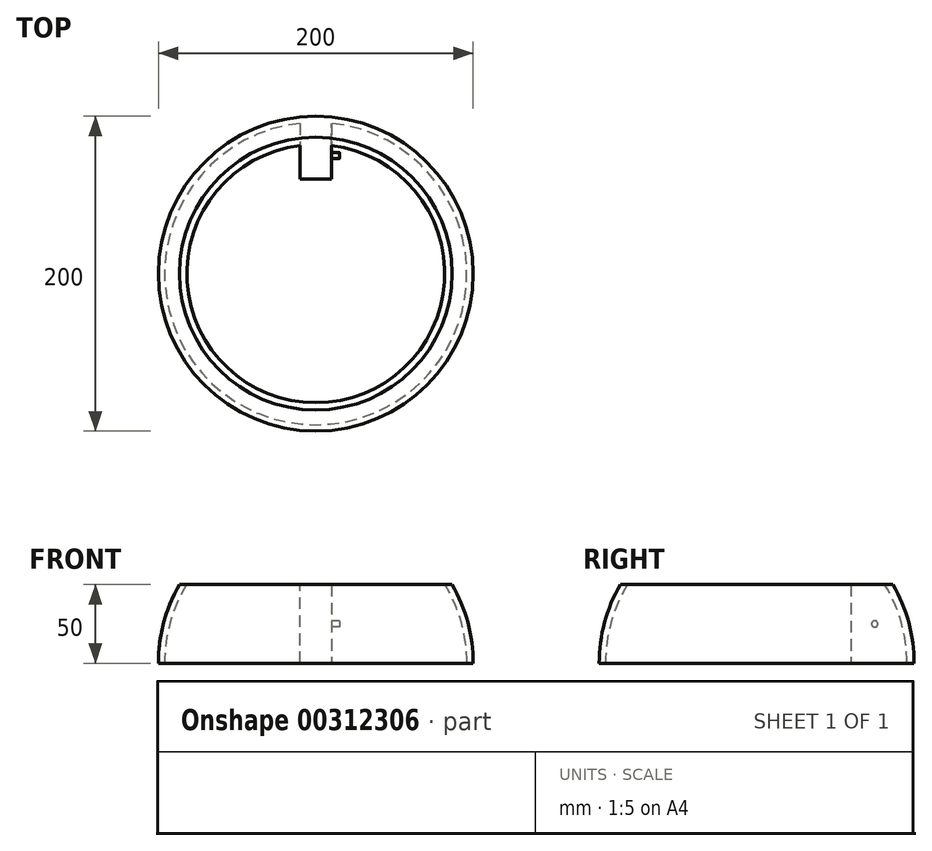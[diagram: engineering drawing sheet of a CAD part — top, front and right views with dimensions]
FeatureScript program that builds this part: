
annotation { "Feature Type Name" : "Feature", "Feature Type Description" : "" }
export const myFeature = defineFeature(function(context is Context, id is Id, definition is map)
    precondition{}
    {
        {
            var Q0;
            Q0=qCreatedBy(makeId("Front.planeOp"),FACE);
            var sketch = newSketch(context, id + "F0", { "sketchPlane" : qUnion([Q0])});
            skCircle(sketch, "E0", {"center": v(0, 0) * mm, "radius": 100 * mm});
            skLineSegment(sketch, "E1", {"start": v(-120.23, 0) * mm, "end": v(127.27, 0) * mm});
            skLineSegment(sketch, "E2", {"start": v(0, 0) * mm, "end": v(0, 106.19) * mm});
            skLineSegment(sketch, "E3", {"start": v(0, 50) * mm, "end": v(113.21, 50) * mm});
            skSolve(sketch);
        }
        {
            var Q0;
            {var subQ0=sQuery(id+"F0.wireOp",EDGE,"E3");var subQ1=sQuery(id+"F0.wireOp",EDGE,"E0");var subQ2=makeQuery(id+"F0.imprint","INTERSECT",VERTEX,{"derivedFrom":[subQ1,subQ0]});Q0=makeQuery(id+"F0.imprint","IMPRINT",FACE,{"disambiguationData":[TD([[makeQuery(id+"F0.imprint","IMPRINT",EDGE,{"disambiguationData":[TD([[subQ2,1.0]])],"derivedFrom":subQ1}),1.0]])]});}
            var Q1;
            Q1=sQuery(id+"F0.wireOp",EDGE,"E2");
            revolve(context, id + "F1", {"entities" : qUnion([Q0]), "axis" : qUnion([Q1]), "revolveType" : RevolveType.FULL});
        }
        {
            var Q0;
            Q0=makeQuery(id+"F1.opRevolve","SWEPT_FACE",FACE,{"disambiguationData":[OSD([sQuery(id+"F0.wireOp",EDGE,"E1")])]});
            var Q1;
            Q1=makeQuery(id+"F1.opRevolve","SWEPT_FACE",FACE,{"disambiguationData":[OSD([sQuery(id+"F0.wireOp",EDGE,"E3")])]});
            shell(context, id + "F2", {"entities" : qUnion([Q0, Q1]), "thickness" : 4 * mm});
        }
        {
            var Q0;
            Q0=qCreatedBy(makeId("Front.planeOp"),FACE);
            cPlane(context, id + "F3", {"entities" : qUnion([Q0]), "cplaneType" : CPlaneType.OFFSET, "offset" : 60 * mm, "oppositeDirection" : true, "width" : 150 * mm, "height" : 150 * mm});
        }
        {
            var Q0;
            Q0=qCreatedBy(id+"F3.planeOp",FACE);
            var sketch = newSketch(context, id + "F4", { "sketchPlane" : qUnion([Q0])});
            skLineSegment(sketch, "E4", {"start": v(-10, 0) * mm, "end": v(-10, 50) * mm});
            skLineSegment(sketch, "E5", {"start": v(10, 50) * mm, "end": v(10, 0) * mm});
            skLineSegment(sketch, "E6", {"start": v(10, 0) * mm, "end": v(-10, 0) * mm});
            skLineSegment(sketch, "E7", {"start": v(0, 0) * mm, "end": v(0, 63.55) * mm, "construction": true});
            skLineSegment(sketch, "E8.0", {"start": v(10, 50) * mm, "end": v(-10, 50) * mm});
            skPoint(sketch, "E9.orphan", {"position": v(86.6, 50) * mm});
            skPoint(sketch, "E10.orphan", {"position": v(-86.6, 50) * mm});
            skSolve(sketch);
        }
        {
            var Q0;
            Q0=makeQuery(id+"F4.imprint","IMPRINT",FACE,{"disambiguationData":[TD([[makeQuery(id+"F4.imprint","IMPRINT",EDGE,{"derivedFrom":sQuery(id+"F4.wireOp",EDGE,"E4")}),-1.0]])]});
            var Q1;
            Q1=makeQuery(id+"F1.opRevolve","SWEPT_FACE",FACE,{"disambiguationData":[OSD([sQuery(id+"F0.wireOp",EDGE,"E0")])]});
            extrude(context, id + "F5", {"entities" : qUnion([Q0]), "operationType" : NewBodyOperationType.ADD, "endBound" : BoundingType.UP_TO_SURFACE, "oppositeDirection" : true, "endBoundEntityFace" : qUnion([Q1]), "depth" : 25 * mm});
        }
        {
            var Q0;
            Q0=makeQuery(id+"F5.opExtrude","SWEPT_FACE",FACE,{"disambiguationData":[OSD([sQuery(id+"F4.wireOp",EDGE,"E5")])]});
            var sketch = newSketch(context, id + "F6", { "sketchPlane" : qUnion([Q0])});
            skCircle(sketch, "E11", {"center": v(75, 25) * mm, "radius": 2 * mm});
            skSolve(sketch);
        }
        {
            var Q0;
            Q0=makeQuery(id+"F6.imprint","IMPRINT",FACE,{"disambiguationData":[TD([[makeQuery(id+"F6.imprint","IMPRINT",EDGE,{"derivedFrom":sQuery(id+"F6.wireOp",EDGE,"E11")}),1.0]])]});
            extrude(context, id + "F7", {"entities" : qUnion([Q0]), "operationType" : NewBodyOperationType.ADD, "depth" : 5 * mm});
        }
    });
